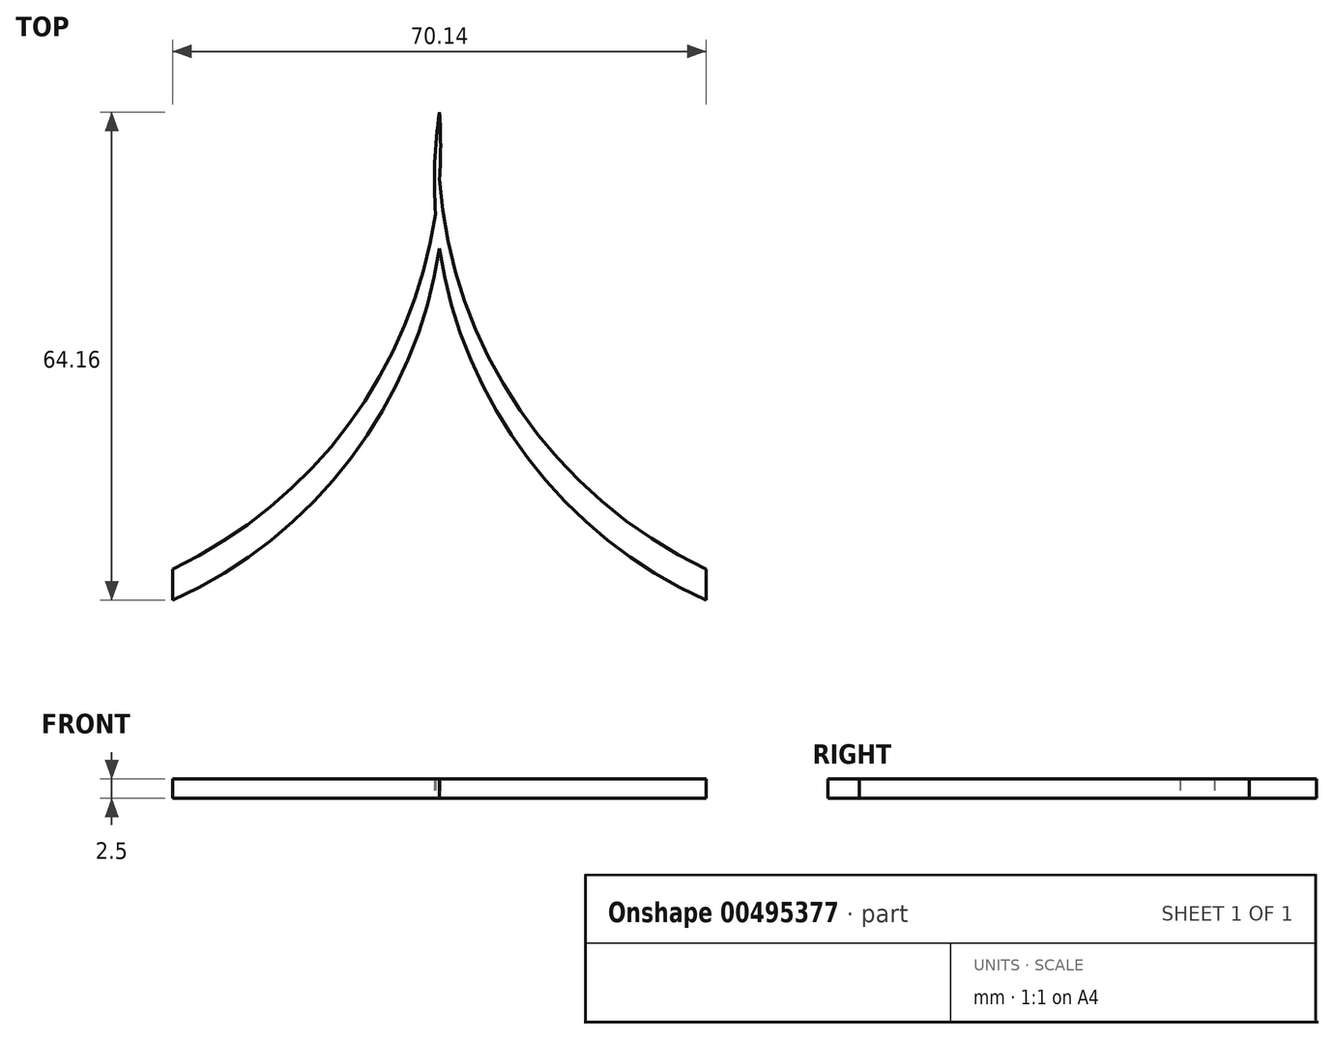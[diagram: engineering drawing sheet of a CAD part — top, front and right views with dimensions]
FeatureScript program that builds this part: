
annotation { "Feature Type Name" : "Feature", "Feature Type Description" : "" }
export const myFeature = defineFeature(function(context is Context, id is Id, definition is map)
    precondition{}
    {
        {
            var Q0;
            Q0=qCreatedBy(makeId("Top.planeOp"),FACE);
            var sketch = newSketch(context, id + "F0", { "sketchPlane" : qUnion([Q0])});
            skArc(sketch, "E0", {"start": v(-35.07, -64.16) * mm, "mid": v(-6.75, -37.97) * mm, "end": v(0, 0) * mm});
            skLineSegment(sketch, "E1", {"start": v(0, 23.13) * mm, "end": v(0, -74.6) * mm, "construction": true});
            skArc(sketch, "E2.MirrorCS", {"start": v(35.07, -64.16) * mm, "mid": v(6.75, -37.97) * mm, "end": v(0, 0) * mm});
            skLineSegment(sketch, "E3", {"start": v(-35.07, -64.16) * mm, "end": v(-35.07, -60.06) * mm});
            skArc(sketch, "E4", {"start": v(-35.07, -60.06) * mm, "mid": v(-8.25, -35.45) * mm, "end": v(0, 0) * mm});
            skArc(sketch, "E5.MirrorCS", {"start": v(35.07, -60.06) * mm, "mid": v(8.25, -35.45) * mm, "end": v(0, 0) * mm});
            skLineSegment(sketch, "E6.MirrorCS", {"start": v(35.07, -64.16) * mm, "end": v(35.07, -60.06) * mm});
            skSolve(sketch);
        }
        {
            var Q0;
            {var subQ5=sQuery(id+"F0.wireOp",EDGE,"E6.MirrorCS");Q0=makeQuery(id+"F0.imprint","IMPRINT",FACE,{"disambiguationData":[TD([[makeQuery(id+"F0.imprint","IMPRINT",EDGE,{"derivedFrom":subQ5}),1.0]])]});}
            var Q1;
            {var subQ0=sQuery(id+"F0.wireOp",EDGE,"E3");Q1=makeQuery(id+"F0.imprint","IMPRINT",FACE,{"disambiguationData":[TD([[makeQuery(id+"F0.imprint","IMPRINT",EDGE,{"derivedFrom":subQ0}),-1.0]])]});}
            var Q2;
            {var subQ0=sQuery(id+"F0.wireOp",EDGE,"E5.MirrorCS");var subQ2=sQuery(id+"F0.wireOp",EDGE,"E0");var subQ4=makeQuery(id+"F0.imprint","INTERSECT",VERTEX,{"derivedFrom":[subQ2,subQ0]});Q2=makeQuery(id+"F0.imprint","IMPRINT",FACE,{"disambiguationData":[TD([[makeQuery(id+"F0.imprint","IMPRINT",EDGE,{"disambiguationData":[TD([[subQ4,-1.0]])],"derivedFrom":subQ0}),-1.0]])]});}
            var Q3;
            {var subQ1=sQuery(id+"F0.wireOp",EDGE,"E4");var subQ2=sQuery(id+"F0.wireOp",EDGE,"E2.MirrorCS");var subQ4=makeQuery(id+"F0.imprint","INTERSECT",VERTEX,{"derivedFrom":[subQ2,subQ1]});Q3=makeQuery(id+"F0.imprint","IMPRINT",FACE,{"disambiguationData":[TD([[makeQuery(id+"F0.imprint","IMPRINT",EDGE,{"disambiguationData":[TD([[subQ4,-1.0]])],"derivedFrom":subQ1}),1.0]])]});}
            var Q4;
            {var subQ0=sQuery(id+"F0.wireOp",EDGE,"E2.MirrorCS");var subQ1=sQuery(id+"F0.wireOp",EDGE,"E0");var subQ2=makeQuery(id+"F0.imprint","INTERSECT",VERTEX,{"derivedFrom":[subQ1,subQ0]});Q4=makeQuery(id+"F0.imprint","IMPRINT",FACE,{"disambiguationData":[TD([[makeQuery(id+"F0.imprint","IMPRINT",EDGE,{"disambiguationData":[TD([[subQ2,-1.0]])],"derivedFrom":subQ1}),1.0]])]});}
            var Q5;
            {var subQ0=sQuery(id+"F0.wireOp",EDGE,"E5.MirrorCS");var subQ1=sQuery(id+"F0.wireOp",EDGE,"E4");var subQ3=makeQuery(id+"F0.imprint","INTERSECT",VERTEX,{"derivedFrom":[subQ1,subQ0]});Q5=makeQuery(id+"F0.imprint","IMPRINT",FACE,{"disambiguationData":[TD([[makeQuery(id+"F0.imprint","IMPRINT",EDGE,{"disambiguationData":[TD([[subQ3,-1.0]])],"derivedFrom":subQ1}),1.0]])]});}
            extrude(context, id + "F1", {"entities" : qUnion([Q0, Q1, Q2, Q3, Q4, Q5]), "depth" : 2.5 * mm});
        }
    });
